FCSTD DOCUMENT  (FreeCAD 0.17R11939 (Git))
Label: fork_steering_tab
License: All rights reserved
LicenseURL: http://en.wikipedia.org/wiki/All_rights_reserved
objects: Sketcher::SketchObject×3, Spreadsheet::Sheet×1
note: 3 computed .brp shape members not serialized (recipe doc carries the construction recipe); baked Part::Feature solids carry a one-line shape summary decoded from their .brp

FEATURE [Sketcher::SketchObject] Sketch
  expr: Constraints[14] = 20mm + Spreadsheet.kerf
  expr: Constraints[38] = Spreadsheet.kerf / 2
  sketch-geometry (13):
    g0: LineSegment StartX=0 StartY=10.6477 StartZ=0 EndX=37.0824 EndY=10.6477 EndZ=0
    g1: LineSegment StartX=0 StartY=-10.6477 StartZ=0 EndX=37.0824 EndY=-10.6477 EndZ=0
    g2: ArcOfCircle CenterX=-7.96992 CenterY=0 CenterZ=0 NormalX=0 NormalY=0 NormalZ=1 Radius=11.7602 StartAngle=5.45702 EndAngle=7.10935
    g3: LineSegment StartX=0 StartY=8.6477 StartZ=0 EndX=0 EndY=10.6477 EndZ=0
    g4: LineSegment StartX=0 StartY=-10.6477 StartZ=0 EndX=0 EndY=-8.6477 EndZ=0
    g5: Circle [constr] CenterX=37.0301 CenterY=0 CenterZ=0 NormalX=0 NormalY=0 NormalZ=1 Radius=5.2
    g6: LineSegment StartX=47.2301 StartY=-0.5 StartZ=0 EndX=47.2301 EndY=0.5 EndZ=0
    g7: ArcOfCircle CenterX=37.0824 CenterY=0.5 CenterZ=0 NormalX=0 NormalY=0 NormalZ=1 Radius=10.1477 StartAngle=0 EndAngle=1.5708
    g8: ArcOfCircle CenterX=37.0824 CenterY=-0.5 CenterZ=0 NormalX=0 NormalY=0 NormalZ=1 Radius=10.1477 StartAngle=4.71239 EndAngle=6.28319
    g9: LineSegment [constr] StartX=42.2301 StartY=0 StartZ=0 EndX=47.2301 EndY=0 EndZ=0
    g10: LineSegment [constr] StartX=37.0301 StartY=5.2 StartZ=0 EndX=37.0301 EndY=10.6477 EndZ=0
    g11: Circle CenterX=37.0301 CenterY=0 CenterZ=0 NormalX=0 NormalY=0 NormalZ=1 Radius=4.5523
    g12: LineSegment [constr] StartX=31.8301 StartY=0 StartZ=0 EndX=32.4778 EndY=0 EndZ=0
  constraints (42):
    c: PointOnObject(g0,g-2)
    c: Horizontal(g0)
    c: PointOnObject(g1,g-2)
    c: Horizontal(g1)
    c: PointOnObject(g2,g-2)
    c: PointOnObject(g2,g-2)
    c: Coincident(g3,g2)
    c: Vertical(g3)
    c: Coincident(g0,g3)
    c: Coincident(g4,g2)
    c: Coincident(g1,g4)
    c: Distance(g3) = 2
    c: Radius(g2) = 11.7602
    c: PointOnObject(g2,g-1)
    c: Distance(g0,g1) = 21.2954
    c: PointOnObject(g5,g-1)
    c: Radius(g5) = 5.2
    c: Distance(g5,g2) = 45
    c: Vertical(g6)
    c: Tangent(g6,g7) = -1.5708
    c: Tangent(g0,g7) = 1.5708
    c: Tangent(g1,g8) = -1.5708
    c: Tangent(g6,g8) = -1.5708
    c: PointOnObject(g9,g5)
    c: PointOnObject(g9,g6)
    c: Horizontal(g9)
    c: Distance(g9) = 5
    c: PointOnObject(g9,g-1)
    c: PointOnObject(g10,g5)
    c: Vertical(g10)
    c: PointOnObject(g10,g0)
    c: Perpendicular(g5,g10)
    c: Distance(g10) = 5.4477
    c: PointOnObject(g12,g5)
    c: PointOnObject(g12,g11)
    c: Horizontal(g12)
    c: Perpendicular(g11,g12)
    c: Coincident(g5,g11)
    c: Distance(g12) = 0.6477
    c: Equal(g4,g3)
    c: Symmetric(g6,g6,g-1)
    c: Distance(g6,g6) = 1
FEATURE [Spreadsheet::Sheet] Spreadsheet
  cells = A1=kerf; B1(kerf)==0.050999999999999997in; C1=diameter of plasma arc; A2=blade_diam; B2(blade_diam)==7in / 8; C2=fork blade tube O.D.
FEATURE [Sketcher::SketchObject] Sketch001
  expr: Constraints[40] = Spreadsheet.kerf / 2
  expr: Constraints[28] = Spreadsheet.kerf / 2
  expr: Constraints[22] = Spreadsheet.blade_diam / 2
  expr: Constraints[61] = Spreadsheet.kerf / 2
  expr: Constraints[17] = Spreadsheet.kerf / 2
  sketch-geometry (20):
    g0: LineSegment StartX=0 StartY=10.8477 StartZ=0 EndX=34.9905 EndY=10.8477 EndZ=0
    g1: LineSegment StartX=0 StartY=-10.8477 StartZ=0 EndX=34.9905 EndY=-10.8477 EndZ=0
    g2: Circle [constr] CenterX=34.9905 CenterY=0 CenterZ=0 NormalX=0 NormalY=0 NormalZ=1 Radius=5.2
    g3: LineSegment [constr] StartX=40.1905 StartY=0 StartZ=0 EndX=45.1905 EndY=0 EndZ=0
    g4: LineSegment [constr] StartX=34.9905 StartY=5.2 StartZ=0 EndX=34.9905 EndY=10.2 EndZ=0
    g5: Circle CenterX=34.9905 CenterY=0 CenterZ=0 NormalX=0 NormalY=0 NormalZ=1 Radius=4.5523
    g6: LineSegment [constr] StartX=29.7905 StartY=0 StartZ=0 EndX=30.4382 EndY=0 EndZ=0
    g7: Circle [constr] CenterX=-10.0095 CenterY=0 CenterZ=0 NormalX=0 NormalY=0 NormalZ=1 Radius=11.1125
    g8: ArcOfCircle CenterX=-10.0095 CenterY=0 CenterZ=0 NormalX=0 NormalY=0 NormalZ=1 Radius=14.7602 StartAngle=0.825562 EndAngle=5.45762
    g9: Circle CenterX=-10.0095 CenterY=0 CenterZ=0 NormalX=0 NormalY=0 NormalZ=1 Radius=10.4648
    g10: LineSegment [constr] StartX=-10.0095 StartY=10.4648 StartZ=0 EndX=-10.0095 EndY=11.1125 EndZ=0
    g11: ArcOfCircle [constr] CenterX=-10.0095 CenterY=0 CenterZ=0 NormalX=0 NormalY=0 NormalZ=1 Radius=14.1125 StartAngle=0.876742 EndAngle=5.40644
    g12: LineSegment [constr] StartX=0 StartY=10.8477 StartZ=0 EndX=-0.982356 EndY=10.8477 EndZ=0
    g13: LineSegment [constr] StartX=0 StartY=-10.8477 StartZ=0 EndX=-0.982356 EndY=-10.8477 EndZ=0
    g14: LineSegment [constr] StartX=-10.0095 StartY=14.1125 StartZ=0 EndX=-10.0095 EndY=14.7602 EndZ=0
    g15: LineSegment [constr] StartX=-21.122 StartY=0 StartZ=0 EndX=-24.122 EndY=0 EndZ=0
    g16: ArcOfCircle [constr] CenterX=34.9905 CenterY=0 CenterZ=0 NormalX=0 NormalY=0 NormalZ=1 Radius=10.2 StartAngle=4.71239 EndAngle=7.85398
    g17: ArcOfCircle CenterX=34.9905 CenterY=0 CenterZ=0 NormalX=0 NormalY=0 NormalZ=1 Radius=10.8477 StartAngle=4.71239 EndAngle=7.85398
    g18: LineSegment [constr] StartX=34.9905 StartY=10.2 StartZ=0 EndX=34.9905 EndY=10.8477 EndZ=0
    g19: LineSegment [constr] StartX=34.9905 StartY=-10.2 StartZ=0 EndX=34.9905 EndY=-10.8477 EndZ=0
  constraints (62):
    c: PointOnObject(g0,g-2)
    c: Horizontal(g0)
    c: PointOnObject(g1,g-2)
    c: Horizontal(g1)
    c: PointOnObject(g2,g-1)
    c: Radius(g2) = 5.2
    c: PointOnObject(g3,g2)
    c: Horizontal(g3)
    c: PointOnObject(g3,g-1)
    c: PointOnObject(g4,g2)
    c: Vertical(g4)
    c: Perpendicular(g2,g4)
    c: PointOnObject(g6,g2)
    c: PointOnObject(g6,g5)
    c: Horizontal(g6)
    c: Perpendicular(g5,g6)
    c: Coincident(g2,g5)
    c: Distance(g6) = 0.6477
    c: Distance(g2,g7) = 45
    c: Coincident(g8,g7)
    c: Coincident(g8,g0)
    c: Coincident(g8,g1)
    c: Radius(g7) = 11.1125
    c: Coincident(g9,g7)
    c: PointOnObject(g10,g9)
    c: PointOnObject(g10,g7)
    c: Vertical(g10)
    c: Perpendicular(g7,g10)
    c: Distance(g10) = 0.6477
    c: Coincident(g11,g7)
    c: Coincident(g12,g0)
    c: Horizontal(g12)
    c: Coincident(g11,g12)
    c: Coincident(g13,g1)
    c: Horizontal(g13)
    c: Coincident(g11,g13)
    c: PointOnObject(g14,g11)
    c: PointOnObject(g14,g8)
    c: Vertical(g14)
    c: Perpendicular(g8,g14)
    c: Distance(g14) = 0.6477
    c: PointOnObject(g15,g7)
    c: PointOnObject(g15,g11)
    c: Horizontal(g15)
    c: Perpendicular(g11,g15)
    c: Equal(g4,g3)
    c: Symmetric(g1,g0,g-1)
    c: Distance(g15) = 3
    c: Coincident(g16,g2)
    c: PointOnObject(g3,g16)
    c: Coincident(g4,g16)
    c: Coincident(g17,g2)
    c: Coincident(g17,g0)
    c: Coincident(g17,g1)
    c: Coincident(g18,g0)
    c: Coincident(g4,g18)
    c: Vertical(g18)
    c: Coincident(g19,g16)
    c: Coincident(g19,g1)
    c: Vertical(g19)
    c: Distance(g4) = 5
    c: Distance(g18) = 0.6477
FEATURE [Sketcher::SketchObject] Sketch002
  sketch-geometry (12):
    g0: Circle [constr] CenterX=0 CenterY=46.0977 CenterZ=0 NormalX=0 NormalY=0 NormalZ=1 Radius=12.7
    g1: ArcOfCircle CenterX=0 CenterY=46.0977 CenterZ=0 NormalX=0 NormalY=0 NormalZ=1 Radius=12.7 StartAngle=3.5798 EndAngle=5.84497
    g2: LineSegment StartX=-11.5 StartY=40.7088 StartZ=0 EndX=-11.5 EndY=-5 EndZ=0
    g3: LineSegment StartX=11.5 StartY=40.7088 StartZ=0 EndX=11.5 EndY=-5 EndZ=0
    g4: LineSegment StartX=-6.5 StartY=-10 StartZ=0 EndX=6.5 EndY=-10 EndZ=0
    g5: LineSegment [constr] StartX=0 StartY=46.0977 StartZ=0 EndX=0 EndY=-10 EndZ=0
    g6: Circle CenterX=0 CenterY=0 CenterZ=0 NormalX=0 NormalY=0 NormalZ=1 Radius=5.25
    g7: LineSegment [constr] StartX=0 StartY=46.0977 StartZ=0 EndX=97.6187 EndY=24.4047 EndZ=0
    g8: LineSegment [constr] StartX=0 StartY=46.0977 StartZ=0 EndX=-21.693 EndY=-51.521 EndZ=0
    g9: ArcOfCircle CenterX=6.5 CenterY=-5 CenterZ=0 NormalX=0 NormalY=0 NormalZ=1 Radius=5 StartAngle=4.71239 EndAngle=6.28319
    g10: ArcOfCircle CenterX=-6.5 CenterY=-5 CenterZ=0 NormalX=0 NormalY=0 NormalZ=1 Radius=5 StartAngle=3.14159 EndAngle=4.71239
    g11: GeomPoint X=0 Y=33.3977 Z=0
  constraints (35):
    c: Radius(g0) = 12.7
    c: PointOnObject(g1,g0)
    c: Coincident(g3,g1)
    c: Parallel(g3,g2)
    c: Coincident(g1,g2)
    c: Perpendicular(g2,g4)
    c: PointOnObject(g5,g4)
    c: Coincident(g0,g5)
    c: Parallel(g5,g2)
    c: PointOnObject(g6,g5)
    c: Radius(g6) = 5.25
    c: Coincident(g1,g0)
    c: Distance(g6,g5) = 10
    c: Coincident(g6,g-1)
    c: Vertical(g2)
    c: Coincident(g7,g0)
    c: Coincident(g8,g0)
    c: Perpendicular(g7,g8)
    c: Distance(g8) = 100
    c: Distance(g7) = 100
    c: Distance(g-1,g7) = 45
    c: Distance(g-1,g8) = 10
    c: Tangent(g4,g9) = -1.5708
    c: Tangent(g3,g9) = 1.5708
    c: Tangent(g4,g10) = -1.5708
    c: Tangent(g2,g10) = -1.5708
    c: Equal(g9,g10)
    c: Distance(g2,g3) = 23
    c: Radius(g9) = 5
    c: Symmetric(g4,g4,g5)
    c: DistanceY(g4,g1) = 50.7088
    c: PointOnObject(g11,g0)
    c: PointOnObject(g11,g5)
    c: DistanceY(g11,g1) = 7.31112
    c: DistanceY(g-1,g1) = 40.7088
